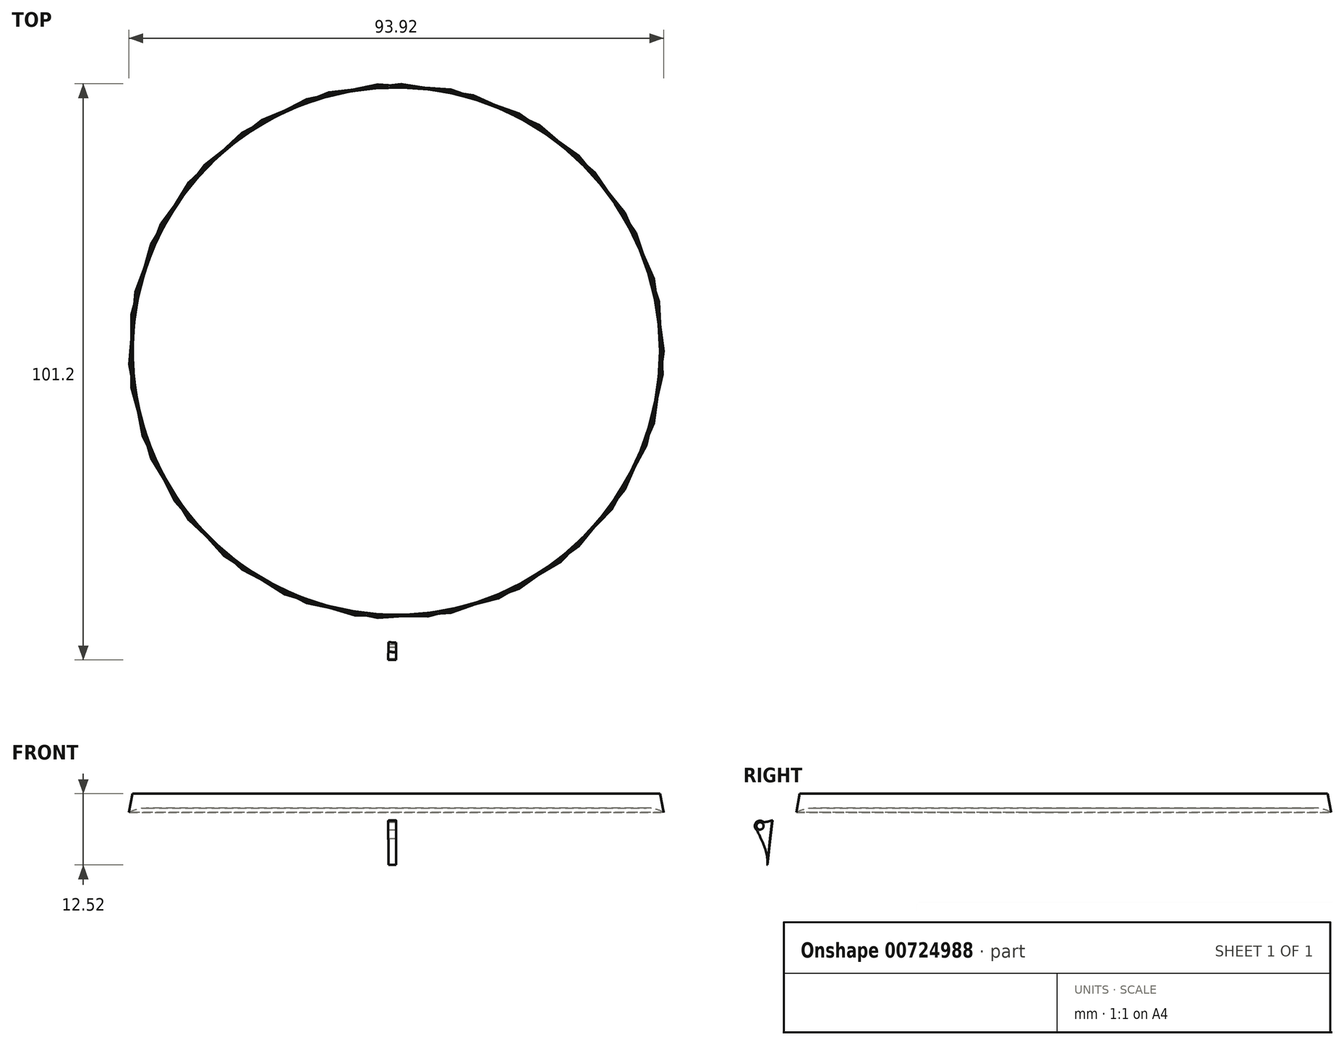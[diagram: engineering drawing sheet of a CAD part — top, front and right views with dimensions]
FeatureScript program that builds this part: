
annotation { "Feature Type Name" : "Feature", "Feature Type Description" : "" }
export const myFeature = defineFeature(function(context is Context, id is Id, definition is map)
    precondition{}
    {
        {
            var Q0;
            Q0=qCreatedBy(makeId("Front.planeOp"),FACE);
            var sketch = newSketch(context, id + "F0", { "sketchPlane" : qUnion([Q0])});
            skLineSegment(sketch, "E0", {"start": v(0, 38.32) * mm, "end": v(49.75, 38.32) * mm});
            skLineSegment(sketch, "E1", {"start": v(0, 38.32) * mm, "end": v(0, 35.82) * mm});
            skLineSegment(sketch, "E2", {"start": v(54.53, 0) * mm, "end": v(52.03, 0) * mm});
            skLineSegment(sketch, "E3", {"start": v(0, 35.82) * mm, "end": v(43.92, 35.82) * mm});
            skLineSegment(sketch, "E4", {"start": v(50.26, 29.84) * mm, "end": v(52.03, 0) * mm});
            skPoint(sketch, "E5.visualSharp", {"position": v(49.9, 35.82) * mm});
            skArc(sketch, "E5.filletArc", {"start": v(50.26, 29.84) * mm, "mid": v(48.28, 34.09) * mm, "end": v(43.92, 35.82) * mm});
            skLineSegment(sketch, "E6", {"start": v(49.75, 38.32) * mm, "end": v(49.75, 33.82) * mm});
            skLineSegment(sketch, "E7", {"start": v(49.76, 33.82) * mm, "end": v(51.26, 33.82) * mm});
            skPoint(sketch, "E8.orphan", {"position": v(51.26, 38.32) * mm});
            skFitSpline(sketch, "E9", {"points": [v(51.26, 33.82) * mm, v(54.53, 0) * mm, v(43.85, 51.24) * mm], "startDerivative": vector(13.3, -113.34) * mm, "endDerivative": vector(-26.67, 139.13) * mm});
            skSolve(sketch);
        }
        {
            var Q0;
            Q0=makeQuery(id+"F0.imprint","IMPRINT",FACE,{"disambiguationData":[TD([[makeQuery(id+"F0.imprint","IMPRINT",EDGE,{"derivedFrom":sQuery(id+"F0.wireOp",EDGE,"E0")}),-1.0]])]});
            var Q1;
            Q1=sQuery(id+"F0.wireOp",EDGE,"E1");
            revolve(context, id + "F1", {"surfaceOperationType" : NewSurfaceOperationType.NEW, "entities" : qUnion([Q0]), "axis" : qUnion([Q1]), "revolveType" : RevolveType.FULL});
        }
        {
            var Q0;
            Q0=qCreatedBy(makeId("Right.planeOp"),FACE);
            var sketch = newSketch(context, id + "F2", { "sketchPlane" : qUnion([Q0])});
            skCircle(sketch, "E10", {"center": v(-53.33, 32.65) * mm, "radius": 0.65 * mm});
            skArc(sketch, "E11", {"start": v(-52.88, 33.44) * mm, "mid": v(-54.05, 33.21) * mm, "end": v(-53.98, 32.02) * mm});
            skLineSegment(sketch, "E12", {"start": v(-51.54, 30.48) * mm, "end": v(-51.3, 32.43) * mm});
            skLineSegment(sketch, "E13", {"start": v(-51.54, 30.48) * mm, "end": v(-52.02, 25.8) * mm});
            skFitSpline(sketch, "E14", {"points": [v(-53.86, 31.91) * mm, v(-52.02, 25.8) * mm, v(-55.6, 18.97) * mm], "startDerivative": vector(6.43, -12.78) * mm, "endDerivative": vector(-9.63, -13.1) * mm});
            skArc(sketch, "E15.filletArc", {"start": v(-53.76, 31.7) * mm, "mid": v(-53.86, 31.87) * mm, "end": v(-53.98, 32.02) * mm});
            skPoint(sketch, "E16.end.orphan", {"position": v(-51.44, 32.43) * mm});
            skLineSegment(sketch, "E17", {"start": v(-51.3, 32.43) * mm, "end": v(-51.16, 33.63) * mm});
            skFitSpline(sketch, "E18", {"points": [v(-51.16, 33.63) * mm, v(-52.8, 33.4) * mm, v(-53.11, 33.95) * mm], "startDerivative": vector(-3.22, -0.95) * mm, "endDerivative": vector(-0.47, 1.8) * mm});
            skSolve(sketch);
        }
        {
            var Q0;
            Q0=makeQuery(id+"F2.imprint","IMPRINT",FACE,{"disambiguationData":[TD([[makeQuery(id+"F2.imprint","IMPRINT",EDGE,{"derivedFrom":sQuery(id+"F2.wireOp",EDGE,"E10")}),-1.0]])]});
            var Q1;
            Q1=makeQuery(id+"F1.opRevolve","SWEPT_FACE",FACE,{"disambiguationData":[OSD([sQuery(id+"F0.wireOp",EDGE,"E9")])]});
            revolve(context, id + "F3", {"operationType" : NewBodyOperationType.ADD, "surfaceOperationType" : NewSurfaceOperationType.NEW, "entities" : qUnion([Q0]), "axis" : qUnion([Q1]), "revolveType" : RevolveType.ONE_DIRECTION, "angle" : 1.5 * degree});
        }
        {
            var Q0;
            Q0=makeQuery(id+"F1.opRevolve","SWEPT_BODY",BODY,{"disambiguationData":[OSD([sQuery(id+"F0.wireOp",EDGE,"E0"),sQuery(id+"F0.wireOp",EDGE,"E1"),sQuery(id+"F0.wireOp",EDGE,"E2"),sQuery(id+"F0.wireOp",EDGE,"E3"),sQuery(id+"F0.wireOp",EDGE,"E4"),sQuery(id+"F0.wireOp",EDGE,"E5.filletArc"),sQuery(id+"F0.wireOp",EDGE,"E6"),sQuery(id+"F0.wireOp",EDGE,"E7"),sQuery(id+"F0.wireOp",EDGE,"E9")])]});
            var Q1;
            Q1=makeQuery(id+"F1.opRevolve","SWEPT_FACE",FACE,{"disambiguationData":[OSD([sQuery(id+"F0.wireOp",EDGE,"E9")])]});
            circularPattern(context, id + "F4", {"entities" : qUnion([Q0]), "axis" : qUnion([Q1]), "angle" : 5 * degree, "instanceCount" : 2, "equalSpace" : true});
        }
    });
